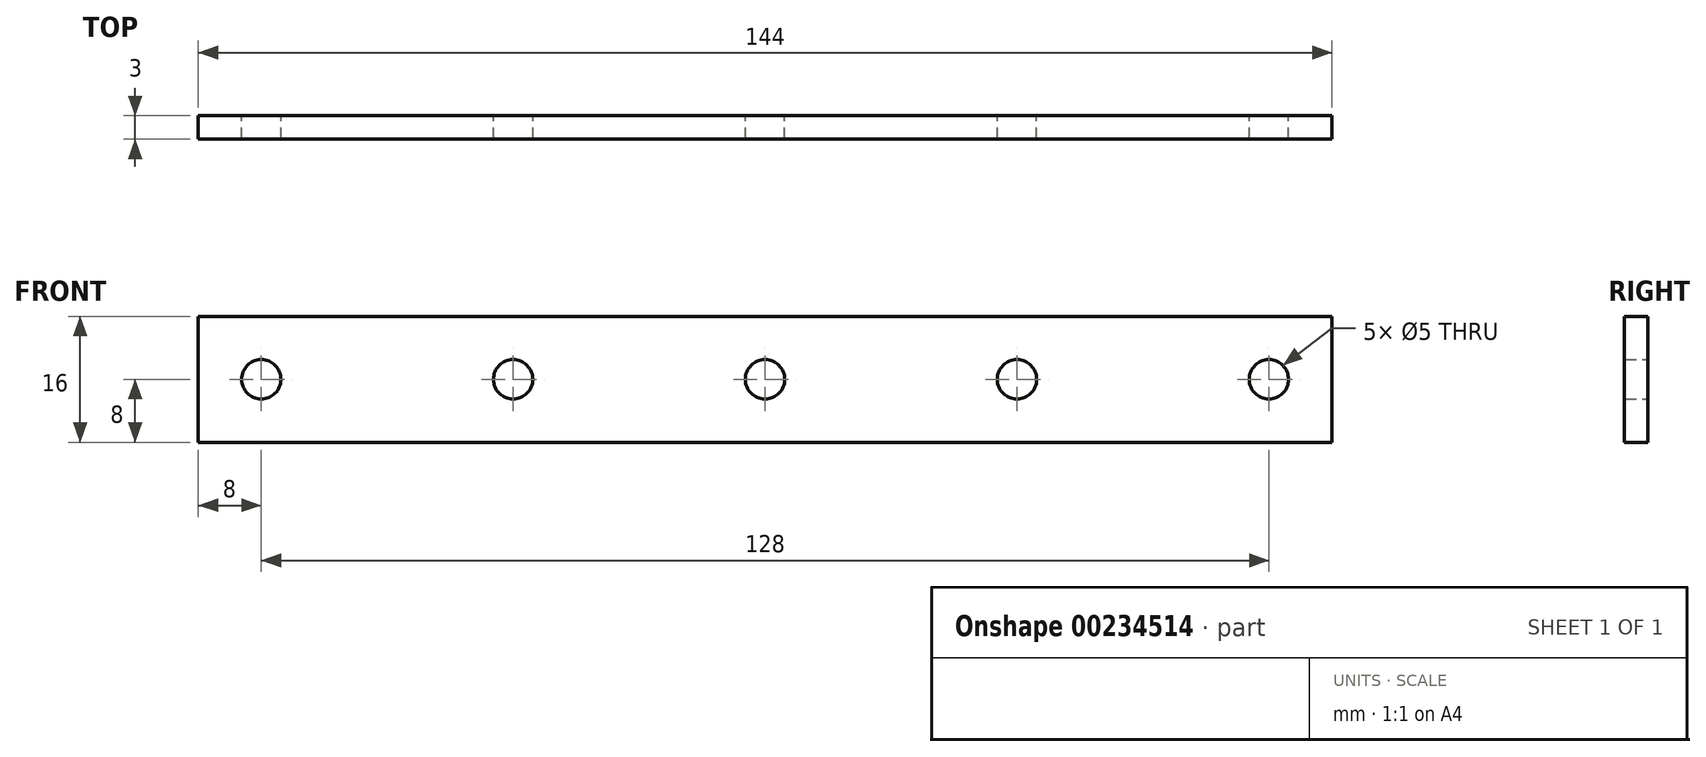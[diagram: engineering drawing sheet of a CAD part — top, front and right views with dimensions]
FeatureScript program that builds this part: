
annotation { "Feature Type Name" : "Feature", "Feature Type Description" : "" }
export const myFeature = defineFeature(function(context is Context, id is Id, definition is map)
    precondition{}
    {
        {
            var Q0;
            Q0=qCreatedBy(makeId("Front.planeOp"), FACE);
            var sketch = newSketch(context, id + "F0", { "sketchPlane" : qUnion([Q0])});
            skLineSegment(sketch, "E0.bottom", {"start": v(72, -8) * mm, "end": v(-72, -8) * mm});
            skLineSegment(sketch, "E0.top", {"start": v(72, 8) * mm, "end": v(-72, 8) * mm});
            skLineSegment(sketch, "E0.left", {"start": v(72, -8) * mm, "end": v(72, 8) * mm});
            skLineSegment(sketch, "E0.right", {"start": v(-72, -8) * mm, "end": v(-72, 8) * mm});
            skPoint(sketch, "E0.middle", {"position": v(0, 0) * mm});
            skCircle(sketch, "E1", {"center": v(-64, 0) * mm, "radius": 2.5 * mm});
            skCircle(sketch, "E2.1.0.0", {"center": v(-32, 0) * mm, "radius": 2.5 * mm});
            skCircle(sketch, "E2.2.0.0", {"center": v(0, 0) * mm, "radius": 2.5 * mm});
            skLineSegment(sketch, "E2.direction1", {"start": v(-64, 0) * mm, "end": v(-32, 0) * mm, "construction": true});
            skCircle(sketch, "E3.0.3.0", {"center": v(32, 0) * mm, "radius": 2.5 * mm});
            skCircle(sketch, "E3.0.4.0", {"center": v(64, 0) * mm, "radius": 2.5 * mm});
            skSolve(sketch);
        }
        {
            var Q0;
            Q0 = qSketchRegion(id + "F0", true);
            extrude(context, id + "F1", {"entities" : qUnion([Q0]), "depth" : 3 * mm, "offsetDistance" : 25 * mm});
        }
    });
